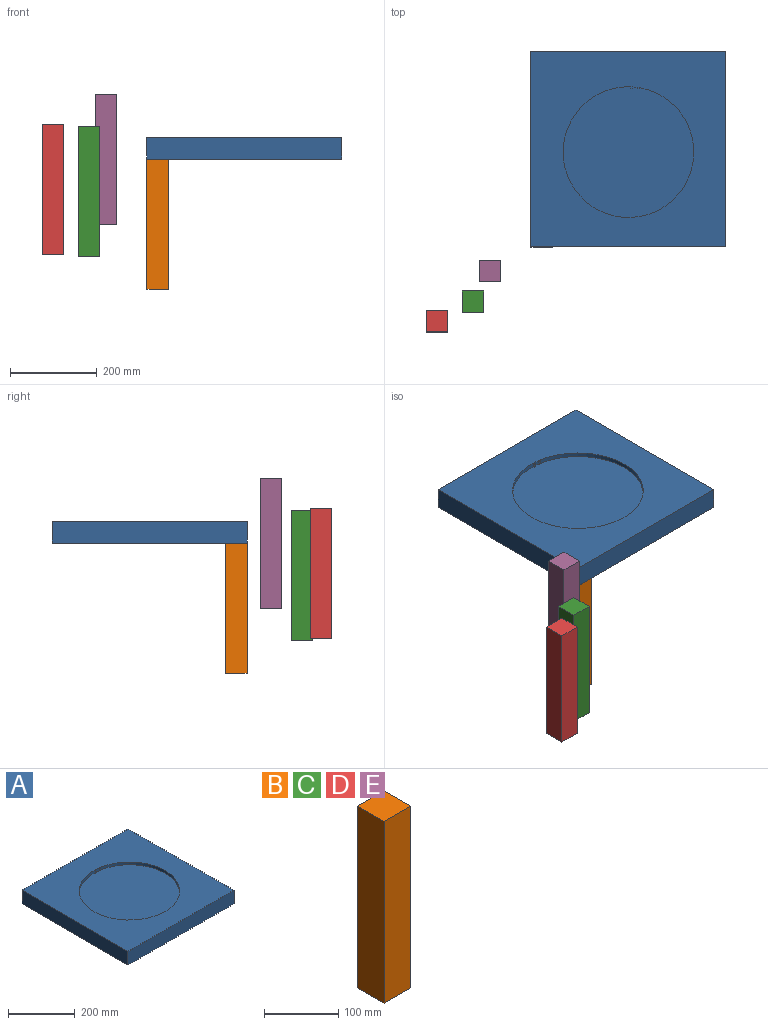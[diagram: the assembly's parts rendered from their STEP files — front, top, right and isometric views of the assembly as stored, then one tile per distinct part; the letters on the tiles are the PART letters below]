
ASSEMBLY  parts=5 mates=1
PART A: 15 faces, bbox 450x450x50 mm
  f0: plane 450x50mm, normal (1,0,0), area 22500mm2, adj f1,f3,f4,f5
  f1: plane 450x50mm, normal (0,1,0), area 22500mm2, adj f0,f2,f4,f5
  f2: plane 450x50mm, normal (-1,0,0), area 22500mm2, adj f1,f3,f4,f5
  f3: plane 450x50mm, normal (0,-1,0), area 22500mm2, adj f0,f2,f4,f5
  f4: plane 450x450mm, normal (0,0,1), area 131070.9mm2, adj f0,f1,f2,f3,f6,f7,f8,f9
  f5: plane 450x450mm, normal (0,0,-1), area 202500mm2, adj f0,f1,f2,f3
  f6: cylinder r=150.81mm len=301.61mm, axis (0,0,1), area 9267.3mm2, adj f4,f7,f13,f14
  f7: plane 10x1.01mm, normal (0.93,-0.36,0), area 10.9mm2, adj f4,f6,f8,f14
  f8: plane 10x3.54mm, normal (0,-1,0), area 35.4mm2, adj f4,f7,f9,f14
  f9: plane 10x1.73mm, normal (-0.93,-0.36,0), area 18.5mm2, adj f4,f8,f10,f14
  f10: cylinder r=150.81mm len=12.02mm, axis (0,0,1), area 120.8mm2, adj f4,f9,f11,f14
  f11: plane 10x2.92mm, normal (1,0,0), area 29.2mm2, adj f4,f10,f12,f14
  f12: plane 10x4.07mm, normal (0,-1,0), area 40.7mm2, adj f4,f11,f13,f14
  f13: plane 10x3.1mm, normal (-1,0,0), area 31mm2, adj f4,f6,f12,f14
  f14: plane 301.61x301.61mm, normal (0,0,1), area 71429.1mm2, adj f6,f7,f8,f9,f10,f11,f12,f13
PART B: 6 faces, bbox 50x50x300 mm
  f0: plane 300x50mm, normal (1,0,0), area 15000mm2, adj f1,f3,f4,f5
  f1: plane 300x50mm, normal (0,1,0), area 15000mm2, adj f0,f2,f4,f5
  f2: plane 300x50mm, normal (-1,0,0), area 15000mm2, adj f1,f3,f4,f5
  f3: plane 300x50mm, normal (0,-1,0), area 15000mm2, adj f0,f2,f4,f5
  f4: plane 50x50mm, normal (0,0,1), area 2500mm2, adj f0,f1,f2,f3
  f5: plane 50x50mm, normal (0,0,-1), area 2500mm2, adj f0,f1,f2,f3
PART C: same geometry as B
PART D: same geometry as B
PART E: same geometry as B
PLACE A t=(50.19,114.97,128.99)mm
PLACE B t=(-147.49,-89.13,-171.01)mm
PLACE C t=(-306.23,-240.82,-96.03)mm
PLACE D t=(-389.58,-285.12,-90.3)mm
PLACE E t=(-267.13,-169.52,-22.93)mm
MATE fastened B.f4 <-> A.f5  axis (0,0,1) through (-174.81,-110.03,128.99)mm
